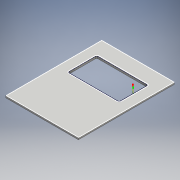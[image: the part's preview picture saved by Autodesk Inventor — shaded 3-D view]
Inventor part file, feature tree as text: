
AUTODESK INVENTOR PART (.ipt)
format: ipt  version: 2016 (Build 200138000, 138)  size: 195,584 bytes
history: native  units: mm
features: extrude x3, sketch x3, fillet x1, projected_geometry x1
ambient origin geometry x8: Origin, YZ Plane, XZ Plane, XY Plane, X Axis, Y Axis, Z Axis, Center Point
bodies: Solid1 (feature_tree)
feature tree (8):
  extrude  "Extrusion1"  Depth=350.0mm
  extrude  "Extrusion2"  Depth=350.0mm
  fillet  "Fillet1"  Radius=132.5mm
  extrude  "Extrusion3"  Depth=8.0mm TaperAngle=0.0deg
  sketch  "Sketch1"  dims[d0=265.0mm d1=350.0mm]
  sketch  "Sketch2"  dims[d2=265.0mm d3=350.0mm d4=132.5mm]
  sketch  "Sketch3"  dims[d5=175.0mm d6=8.0mm d7=0.0mm d8=193.0mm d9=111.0mm d10=96.5mm d11=1.0mm d12=0.0mm d13=8.0mm d14=3.5mm d15=1.0mm d16=0.0mm d17=10.0mm]
  projected_geometry  "Projected Loop1"
